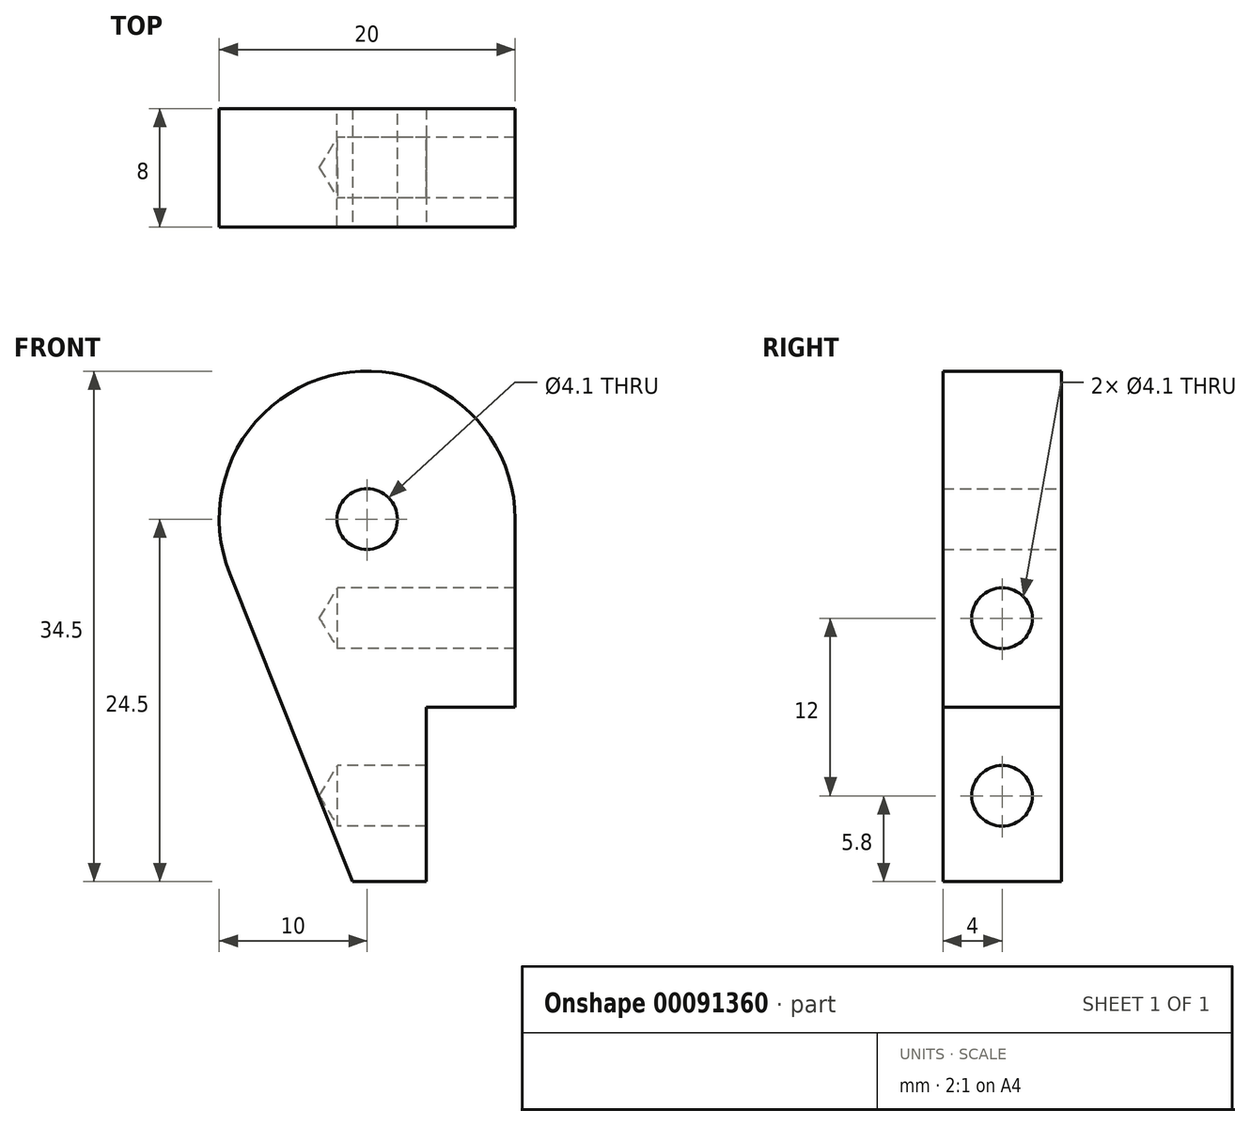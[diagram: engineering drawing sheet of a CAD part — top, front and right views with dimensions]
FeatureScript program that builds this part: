
annotation { "Feature Type Name" : "Feature", "Feature Type Description" : "" }
export const myFeature = defineFeature(function(context is Context, id is Id, definition is map)
    precondition{}
    {
        {
            var Q0;
            Q0=qCreatedBy(makeId("Front.planeOp"),FACE);
            var sketch = newSketch(context, id + "F0", { "sketchPlane" : qUnion([Q0])});
            skArc(sketch, "E0", {"start": v(10, 0) * mm, "mid": v(-1.89, 9.82) * mm, "end": v(-9.29, -3.7) * mm});
            skLineSegment(sketch, "E1", {"start": v(10, 0) * mm, "end": v(10, -12.7) * mm});
            skLineSegment(sketch, "E2", {"start": v(4, -24.5) * mm, "end": v(-1, -24.5) * mm});
            skLineSegment(sketch, "E3", {"start": v(-1, -24.5) * mm, "end": v(-9.29, -3.7) * mm});
            skLineSegment(sketch, "E4", {"start": v(4, -24.5) * mm, "end": v(4, -12.7) * mm});
            skLineSegment(sketch, "E5", {"start": v(4, -12.7) * mm, "end": v(10, -12.7) * mm});
            skSolve(sketch);
        }
        {
            var Q0;
            Q0 = qSketchRegion(id + "F0", true);
            extrude(context, id + "F1", {"entities" : qUnion([Q0]), "oppositeDirection" : true, "depth" : 8 * mm});
        }
        {
            var Q0;
            Q0=sQuery(id+"F0.wireOp",VERTEX,"E0.center");
            var Q1;
            Q1=makeQuery(id+"F1.opExtrude","SWEPT_BODY",BODY,{"disambiguationData":[OSD([sQuery(id+"F0.wireOp",EDGE,"E0"),sQuery(id+"F0.wireOp",EDGE,"E1"),sQuery(id+"F0.wireOp",EDGE,"E2"),sQuery(id+"F0.wireOp",EDGE,"E3")])]});
            hole(context, id + "F2", {"style" : HoleStyle.SIMPLE, "endStyle" : HoleEndStyle.THROUGH, "standardTappedOrClearance" : lookupTablePath({ "standard" : "ISO", "engagement" : "75%", "pitch" : "0.9 mm", "size" : "M5", "type" : "Tapped" }), "standardBlindInLast" : lookupTablePath({ "standard" : "ISO", "engagement" : "75%", "pitch" : "0.9 mm", "size" : "M5", "type" : "Tapped" }), "holeDiameter" : 4.1 * mm, "locations" : qUnion([Q0]), "scope" : qUnion([Q1]), "isTappedThrough" : true, "showTappedDepth" : true, "startStyle" : HoleStartStyle.SKETCH});
        }
        {
            var Q0;
            Q0=makeQuery(id+"F1.opExtrude","SWEPT_FACE",FACE,{"disambiguationData":[OSD([sQuery(id+"F0.wireOp",EDGE,"E1")])]});
            var sketch = newSketch(context, id + "F3", { "sketchPlane" : qUnion([Q0])});
            skLineSegment(sketch, "E6", {"start": v(4, 0) * mm, "end": v(4, -24.5) * mm, "construction": true});
            skPoint(sketch, "E7", {"position": v(4, -18.7) * mm});
            skPoint(sketch, "E8", {"position": v(4, -6.7) * mm});
            skSolve(sketch);
        }
        {
            var Q0;
            Q0=sQuery(id+"F3.wireOp",VERTEX,"E7");
            var Q1;
            Q1=sQuery(id+"F3.wireOp",VERTEX,"E8");
            var Q2;
            Q2=makeQuery(id+"F1.opExtrude","SWEPT_BODY",BODY,{"disambiguationData":[OSD([sQuery(id+"F0.wireOp",EDGE,"E0"),sQuery(id+"F0.wireOp",EDGE,"E1"),sQuery(id+"F0.wireOp",EDGE,"E2"),sQuery(id+"F0.wireOp",EDGE,"E3")])]});
            hole(context, id + "F4", {"style" : HoleStyle.SIMPLE, "endStyle" : HoleEndStyle.BLIND, "standardTappedOrClearance" : lookupTablePath({ "standard" : "ISO", "engagement" : "75%", "pitch" : "0.9 mm", "size" : "M5", "type" : "Tapped" }), "standardBlindInLast" : lookupTablePath({ "standard" : "ISO", "engagement" : "75%", "pitch" : "0.9 mm", "size" : "M5", "type" : "Tapped" }), "holeDiameter" : 4.1 * mm, "holeDepth" : 12 * mm, "locations" : qUnion([Q0, Q1]), "scope" : qUnion([Q2]), "startStyle" : HoleStartStyle.SKETCH});
        }
    });
